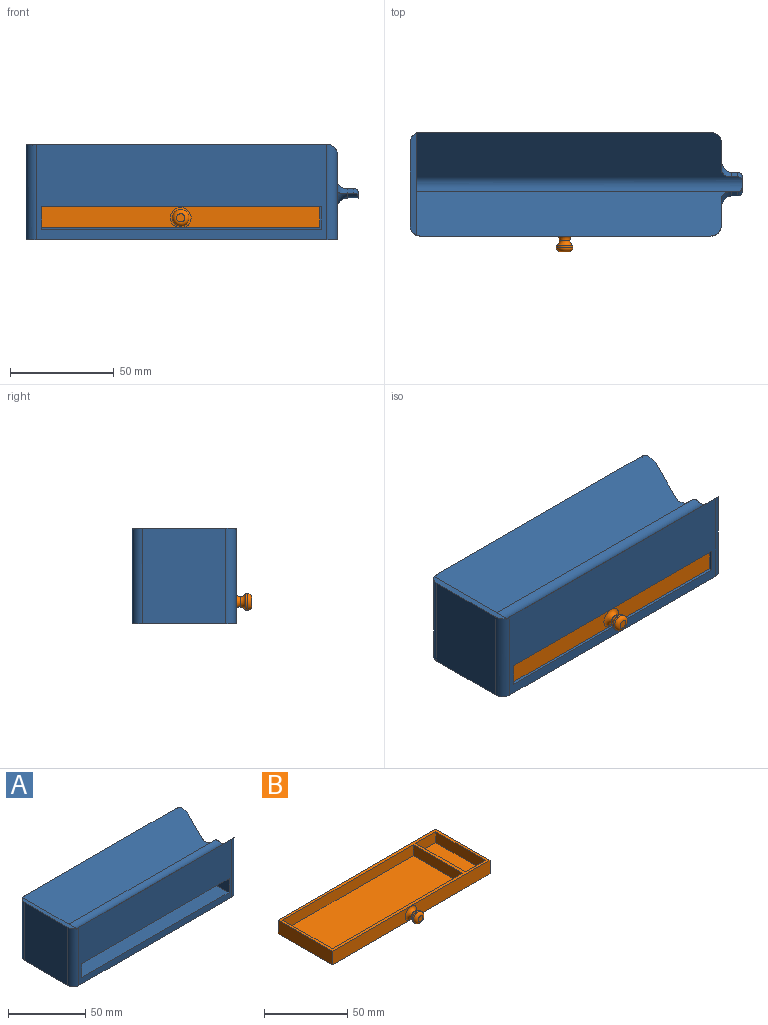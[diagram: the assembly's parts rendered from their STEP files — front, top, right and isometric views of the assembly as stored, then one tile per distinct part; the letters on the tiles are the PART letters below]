
ASSEMBLY  parts=2 mates=1
PART A: 28 faces, bbox 160x50x46 mm
  f0: plane 140x46mm, normal (0,-1,0), area 4955mm2, adj f4,f5,f6,f7,f8,f11,f25,f26
  f1: plane 140x46mm, normal (0,1,0), area 6440mm2, adj f4,f12,f23,f24
  f2: plane 46x40mm, normal (-1,0,0), area 1840mm2, adj f4,f10,f23,f25
  f3: plane 41x40mm, normal (1,0,0), area 1055.5mm2, adj f4,f11,f12,f19,f20,f24,f26,f27
  f4: plane 150x50mm, normal (0,0,-1), area 7478.5mm2, adj f0,f1,f2,f3,f23,f24,f25,f26
  f5: plane 135x47mm, normal (0,0,-1), area 6345mm2, adj f0,f6,f8,f9
  f6: plane 47x11mm, normal (1,0,0), area 517mm2, adj f0,f5,f7,f9
  f7: plane 135x47mm, normal (0,0,1), area 6345mm2, adj f0,f6,f8,f9
  f8: plane 47x11mm, normal (-1,0,0), area 517mm2, adj f0,f5,f7,f9
  f9: plane 135x11mm, normal (0,-1,0), area 1485mm2, adj f5,f6,f7,f8
  f10: plane 49.17x3mm, normal (0,0,1), area 139.8mm2, adj f2,f13,f23,f25
  f11: plane 152x21.46mm, normal (0,0.71,0.71), area 4459.6mm2, adj f0,f3,f13,f14,f20,f25,f26
  f12: plane 152x21.46mm, normal (0,-0.71,0.71), area 4459.6mm2, adj f1,f3,f13,f14,f19,f23,f24
  f13: plane 49.17x22.93mm, normal (1,0,0), area 619.5mm2, adj f10,f11,f12,f14,f23,f25
  f14: cylinder r=5mm len=157mm, axis (-1,0,0), area 1231.3mm2, adj f11,f12,f13,f15,f17,f18,f21,f22
  f15: plane 3x2.12mm, normal (0,-0.71,0.71), area 9mm2, adj f14,f16,f20,f22
  f16: cylinder r=8mm len=11.31mm, axis (-1,0,0), area 61.1mm2, adj f15,f17,f18,f21,f22,f27
  f17: plane 3x2.12mm, normal (0,0.71,0.71), area 9mm2, adj f14,f16,f19,f21
  f18: plane 8.13x3.35mm, normal (1,0,0), area 18.4mm2, adj f14,f16,f21,f22
  f19: cylinder r=5mm len=8.49mm, axis (0,-0.71,0.71), area 35.9mm2, adj f3,f12,f17,f27
  f20: cylinder r=5mm len=8.49mm, axis (0,-0.71,-0.71), area 35.9mm2, adj f3,f11,f15,f27
  f21: cylinder r=2mm len=3.83mm, axis (0,0.71,-0.71), area 9.5mm2, adj f14,f16,f17,f18
  f22: cylinder r=2mm len=3.83mm, axis (0,0.71,0.71), area 9.5mm2, adj f14,f15,f16,f18
  f23: cylinder r=5mm len=46mm, axis (0,0,1), area 361mm2, adj f1,f2,f4,f10,f12,f13
  f24: cylinder r=5mm len=46mm, axis (0,0,-1), area 347mm2, adj f1,f3,f4,f12
  f25: cylinder r=5mm len=46mm, axis (0,0,-1), area 361mm2, adj f0,f2,f4,f10,f11,f13
  f26: cylinder r=5mm len=46mm, axis (0,0,1), area 347mm2, adj f0,f3,f4,f11
  f27: torus R=13mm, axis (1,0,0), area 150.1mm2, adj f3,f16,f19,f20
PART B: 23 faces, bbox 134.1x54.1x10.9 mm
  f0: plane 17x8mm, normal (0,-1,0), area 136mm2, adj f2,f3,f19,f22
  f1: plane 17x8mm, normal (0,1,0), area 136mm2, adj f2,f3,f19,f22
  f2: plane 42x17mm, normal (0,0,1), area 714mm2, adj f0,f1,f19,f22
  f3: plane 134x46mm, normal (0,0,1), area 788mm2, adj f0,f1,f4,f5,f6,f7,f16,f17
  f4: plane 134x10mm, normal (0,1,0), area 1340mm2, adj f3,f5,f7,f8
  f5: plane 46x10mm, normal (-1,0,0), area 460mm2, adj f3,f4,f6,f8
  f6: plane 134x10mm, normal (0,-1,0), area 1262.8mm2, adj f3,f5,f7,f8,f12
  f7: plane 46x10mm, normal (1,0,0), area 460mm2, adj f3,f4,f6,f8
  f8: plane 134.05x46.05mm, normal (0,0,-1), area 6164mm2, adj f4,f5,f6,f7,f13
  f9: cylinder r=2.5mm len=5mm, axis (0,1,0), area 3.3mm2, adj f12,f13,f14
  f10: cylinder r=4mm len=8mm, axis (0,1,0), area 25.1mm2, adj f14,f15
  f11: plane 4x4mm, normal (0,-1,0), area 12.6mm2, adj f15
  f12: torus R=5mm, axis (0,1,0), area 72.5mm2, adj f6,f9,f13
  f13: bspline ~5.43x2.82mm, area 10.3mm2, adj f8,f9,f12
  f14: torus R=5mm, axis (0,-1,0), area 55.1mm2, adj f9,f10
  f15: torus R=2mm, axis (0,-1,0), area 64.6mm2, adj f10,f11
  f16: plane 111x8mm, normal (0,-1,0), area 888mm2, adj f3,f17,f20,f21
  f17: plane 42x8mm, normal (1,0,0), area 336mm2, adj f3,f16,f18,f20
  f18: plane 111x8mm, normal (0,1,0), area 888mm2, adj f3,f17,f20,f21
  f19: plane 42x8mm, normal (-1,0,0), area 336mm2, adj f0,f1,f2,f3
  f20: plane 111x42mm, normal (0,0,1), area 4662mm2, adj f16,f17,f18,f21
  f21: plane 42x8mm, normal (-1,0,0), area 336mm2, adj f3,f16,f18,f20
  f22: plane 42x8mm, normal (1,0,0), area 336mm2, adj f0,f1,f2,f3
PLACE A t=(-101.43,-71.44,-59.28)mm fixed
PLACE B t=(-101.89,-72.94,-53.28)mm
MATE slider A.f8 <-> B.f7  axis (-1,0,0) through (-33.93,-72.94,-48.78)mm
